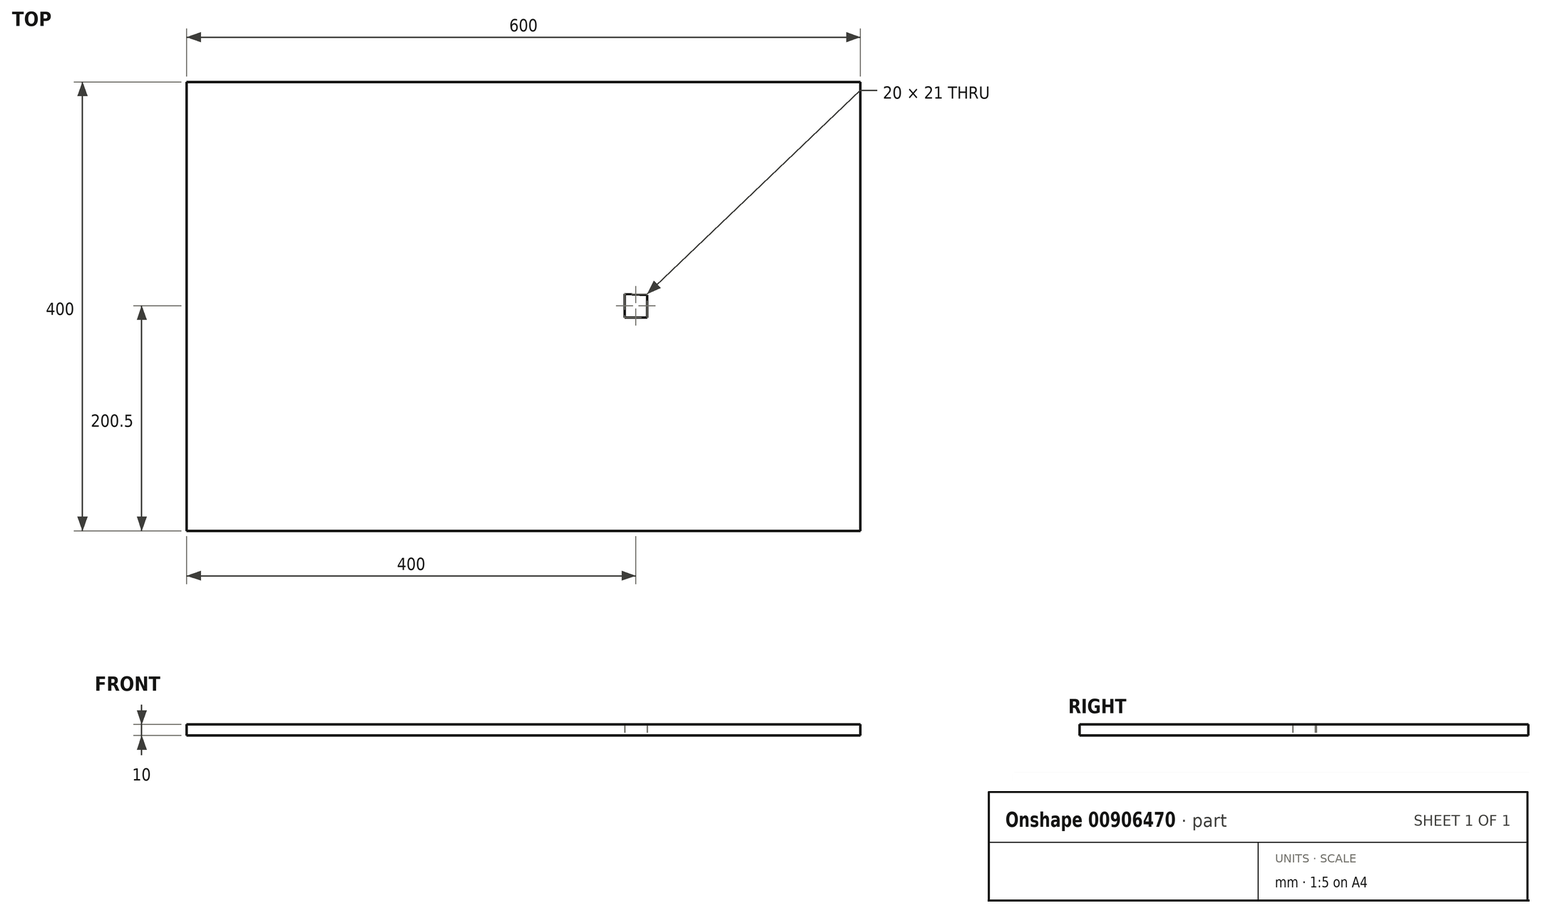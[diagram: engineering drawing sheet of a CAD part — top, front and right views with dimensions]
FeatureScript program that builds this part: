
annotation { "Feature Type Name" : "Feature", "Feature Type Description" : "" }
export const myFeature = defineFeature(function(context is Context, id is Id, definition is map)
    precondition{}
    {
        {
            var Q0;
            Q0=qCreatedBy(makeId("Top.planeOp"),FACE);
            var sketch = newSketch(context, id + "F0", { "sketchPlane" : qUnion([Q0])});
            skLineSegment(sketch, "E0.bottom", {"start": v(-400, 200) * mm, "end": v(200, 200) * mm});
            skLineSegment(sketch, "E0.top", {"start": v(-400, -200) * mm, "end": v(200, -200) * mm});
            skLineSegment(sketch, "E0.left", {"start": v(-400, 200) * mm, "end": v(-400, -200) * mm});
            skLineSegment(sketch, "E0.right", {"start": v(200, 200) * mm, "end": v(200, -200) * mm});
            skLineSegment(sketch, "E1.bottom", {"start": v(-10, 11) * mm, "end": v(10, 10) * mm});
            skLineSegment(sketch, "E1.top", {"start": v(-10, -10) * mm, "end": v(10, -10) * mm});
            skLineSegment(sketch, "E1.left", {"start": v(-10, 11) * mm, "end": v(-10, -10) * mm});
            skLineSegment(sketch, "E1.right", {"start": v(10, 10) * mm, "end": v(10, -10) * mm});
            skSolve(sketch);
        }
        {
            var Q0;
            Q0=makeQuery(id+"F0.imprint","IMPRINT",FACE,{"disambiguationData":[TD([[makeQuery(id+"F0.imprint","IMPRINT",EDGE,{"derivedFrom":sQuery(id+"F0.wireOp",EDGE,"E0.bottom")}),-1.0]])]});
            extrude(context, id + "F1", {"entities" : qUnion([Q0]), "depth" : 10 * mm, "offsetDistance" : 25 * mm});
        }
    });
